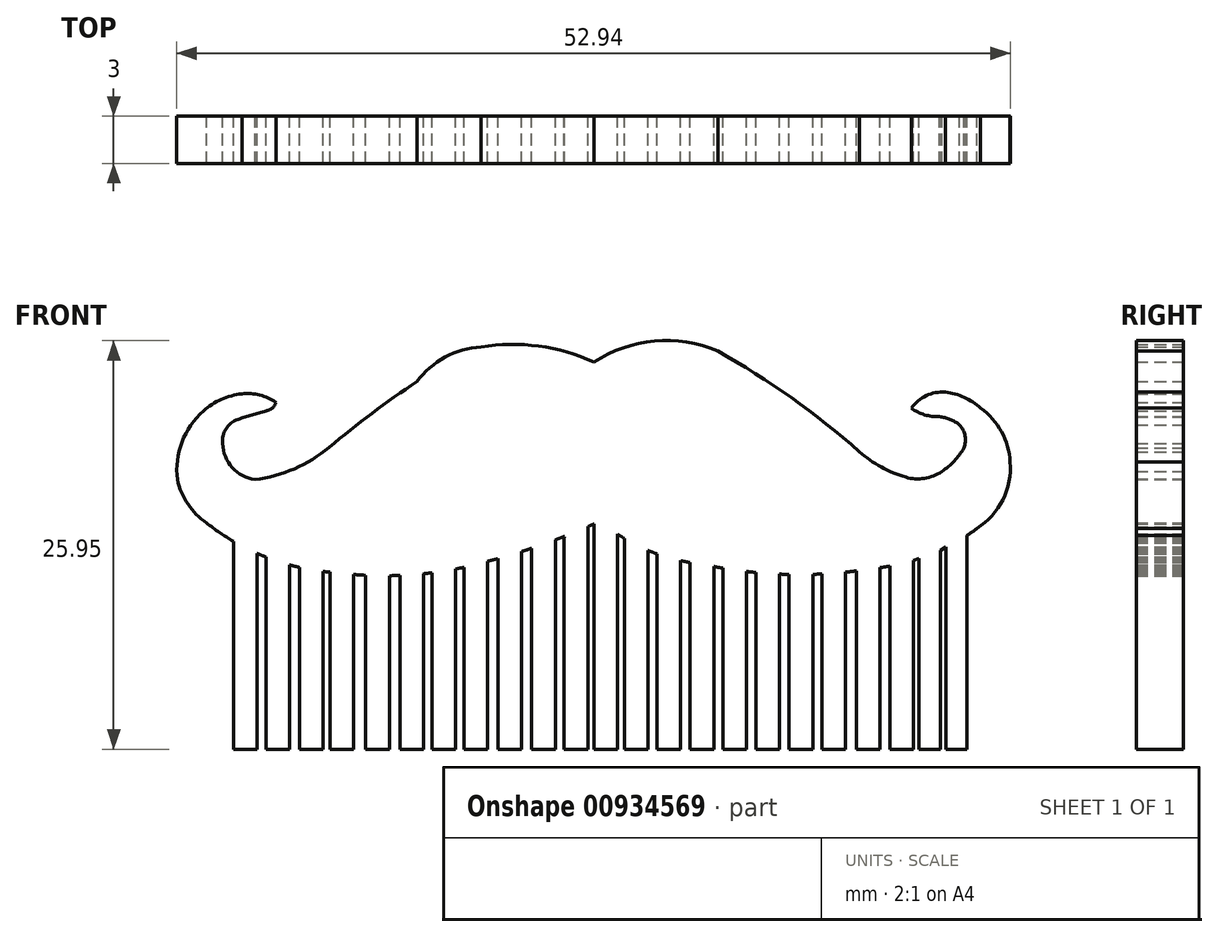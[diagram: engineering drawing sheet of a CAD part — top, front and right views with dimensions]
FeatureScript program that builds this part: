
annotation { "Feature Type Name" : "Feature", "Feature Type Description" : "" }
export const myFeature = defineFeature(function(context is Context, id is Id, definition is map)
    precondition{}
    {
        {
            var Q0;
            Q0=qCreatedBy(makeId("Front.planeOp"),FACE);
            var sketch = newSketch(context, id + "F0", { "sketchPlane" : qUnion([Q0])});
            skArc(sketch, "E0", {"start": v(10.65, 7.83) * mm, "mid": v(6.63, 8.47) * mm, "end": v(2.79, 7.13) * mm});
            skArc(sketch, "E1", {"start": v(2.79, 7.13) * mm, "mid": v(-0.72, 8.15) * mm, "end": v(-4.38, 8.1) * mm});
            skArc(sketch, "E2", {"start": v(-4.38, 8.1) * mm, "mid": v(-6.67, 7.45) * mm, "end": v(-8.46, 5.9) * mm});
            skArc(sketch, "E3", {"start": v(-8.46, 5.9) * mm, "mid": v(-11.3, 3.88) * mm, "end": v(-14.03, 1.72) * mm});
            skArc(sketch, "E4", {"start": v(-18.74, -0.33) * mm, "mid": v(-16.24, 0.36) * mm, "end": v(-14.03, 1.72) * mm});
            skArc(sketch, "E5", {"start": v(-20.8, 1.96) * mm, "mid": v(-20.18, 0.44) * mm, "end": v(-18.74, -0.33) * mm});
            skArc(sketch, "E6", {"start": v(-19.83, 3.5) * mm, "mid": v(-20.58, 2.9) * mm, "end": v(-20.8, 1.96) * mm});
            skArc(sketch, "E7", {"start": v(-18.03, 4.04) * mm, "mid": v(-18.94, 3.78) * mm, "end": v(-19.83, 3.5) * mm});
            skArc(sketch, "E8", {"start": v(-18.03, 4.04) * mm, "mid": v(-17.64, 4.22) * mm, "end": v(-17.4, 4.58) * mm});
            skArc(sketch, "E9", {"start": v(-17.4, 4.58) * mm, "mid": v(-18.44, 5.05) * mm, "end": v(-19.57, 5.12) * mm});
            skArc(sketch, "E10", {"start": v(-19.57, 5.12) * mm, "mid": v(-20.88, 4.78) * mm, "end": v(-22.02, 4.04) * mm});
            skArc(sketch, "E11", {"start": v(-22.02, 4.04) * mm, "mid": v(-23.38, 2.05) * mm, "end": v(-23.67, -0.33) * mm});
            skArc(sketch, "E12", {"start": v(-23.67, -0.33) * mm, "mid": v(-23, -1.88) * mm, "end": v(-21.82, -3.08) * mm});
            skArc(sketch, "E13", {"start": v(-21.82, -3.08) * mm, "mid": v(-20.98, -3.7) * mm, "end": v(-20.11, -4.24) * mm});
            skArc(sketch, "E14", {"start": v(-12.47, -6.36) * mm, "mid": v(-12.09, -6.38) * mm, "end": v(-11.7, -6.4) * mm});
            skArc(sketch, "E15", {"start": v(-3.96, -5.52) * mm, "mid": v(-3.63, -5.43) * mm, "end": v(-3.3, -5.34) * mm});
            skArc(sketch, "E16", {"start": v(4.29, -3.8) * mm, "mid": v(4.5, -3.93) * mm, "end": v(4.73, -4.07) * mm});
            skArc(sketch, "E17", {"start": v(10.4, -5.84) * mm, "mid": v(10.68, -5.9) * mm, "end": v(10.97, -5.95) * mm});
            skArc(sketch, "E18", {"start": v(20.96, -5.92) * mm, "mid": v(21.26, -5.88) * mm, "end": v(21.57, -5.83) * mm});
            skArc(sketch, "E19", {"start": v(27.11, -3.43) * mm, "mid": v(28.75, -1.6) * mm, "end": v(29.22, 0.8) * mm});
            skArc(sketch, "E20", {"start": v(29.22, 0.8) * mm, "mid": v(28.67, 2.72) * mm, "end": v(27.35, 4.2) * mm});
            skArc(sketch, "E21", {"start": v(27.35, 4.2) * mm, "mid": v(26.3, 4.9) * mm, "end": v(25.1, 5.24) * mm});
            skArc(sketch, "E22", {"start": v(25.1, 5.24) * mm, "mid": v(23.9, 5) * mm, "end": v(22.95, 4.2) * mm});
            skArc(sketch, "E23", {"start": v(22.95, 4.2) * mm, "mid": v(23.8, 3.8) * mm, "end": v(24.73, 3.67) * mm});
            skArc(sketch, "E24", {"start": v(26.01, 3.16) * mm, "mid": v(25.4, 3.5) * mm, "end": v(24.73, 3.67) * mm});
            skArc(sketch, "E25", {"start": v(26.28, 1.68) * mm, "mid": v(26.36, 2.46) * mm, "end": v(26.01, 3.16) * mm});
            skArc(sketch, "E26", {"start": v(24.88, 0.2) * mm, "mid": v(25.67, 0.85) * mm, "end": v(26.28, 1.68) * mm});
            skArc(sketch, "E27", {"start": v(22.6, -0.17) * mm, "mid": v(23.78, -0.25) * mm, "end": v(24.88, 0.2) * mm});
            skArc(sketch, "E28", {"start": v(19.65, 1.43) * mm, "mid": v(21.03, 0.47) * mm, "end": v(22.6, -0.17) * mm});
            skArc(sketch, "E29", {"start": v(19.65, 1.43) * mm, "mid": v(15.32, 4.88) * mm, "end": v(10.65, 7.83) * mm});
            skLineSegment(sketch, "E30", {"start": v(4.73, -4.07) * mm, "end": v(4.73, -17.45) * mm});
            skLineSegment(sketch, "E31", {"start": v(6.23, -17.45) * mm, "end": v(6.23, -4.82) * mm});
            skLineSegment(sketch, "E32", {"start": v(8.9, -17.45) * mm, "end": v(8.9, -5.55) * mm});
            skLineSegment(sketch, "E33", {"start": v(10.4, -17.45) * mm, "end": v(10.4, -5.84) * mm});
            skLineSegment(sketch, "E34", {"start": v(13.07, -17.45) * mm, "end": v(13.07, -6.23) * mm});
            skLineSegment(sketch, "E35", {"start": v(14.58, -17.45) * mm, "end": v(14.58, -6.33) * mm});
            skLineSegment(sketch, "E36", {"start": v(17.28, -17.45) * mm, "end": v(17.28, -6.36) * mm});
            skLineSegment(sketch, "E37", {"start": v(18.78, -17.45) * mm, "end": v(18.78, -6.2) * mm});
            skLineSegment(sketch, "E38", {"start": v(21.57, -17.45) * mm, "end": v(21.57, -5.82) * mm});
            skLineSegment(sketch, "E39", {"start": v(23.07, -17.45) * mm, "end": v(23.07, -5.47) * mm});
            skLineSegment(sketch, "E40", {"start": v(26.46, -17.45) * mm, "end": v(26.46, -4.36) * mm});
            skLineSegment(sketch, "E41.MirrorCS", {"start": v(2.4, -3.32) * mm, "end": v(2.4, -17.45) * mm});
            skLineSegment(sketch, "E42.MirrorCS", {"start": v(0.9, -17.45) * mm, "end": v(0.9, -4.04) * mm});
            skLineSegment(sketch, "E43.MirrorCS", {"start": v(-1.8, -17.45) * mm, "end": v(-1.8, -4.9) * mm});
            skLineSegment(sketch, "E44.MirrorCS", {"start": v(-6, -17.45) * mm, "end": v(-6, -6.04) * mm});
            skLineSegment(sketch, "E45.MirrorCS", {"start": v(-7.5, -17.45) * mm, "end": v(-7.5, -6.23) * mm});
            skLineSegment(sketch, "E46.MirrorCS", {"start": v(-10.2, -17.45) * mm, "end": v(-10.2, -6.36) * mm});
            skLineSegment(sketch, "E47.MirrorCS", {"start": v(-11.7, -17.45) * mm, "end": v(-11.7, -6.32) * mm});
            skLineSegment(sketch, "E48.MirrorCS", {"start": v(-14.4, -17.45) * mm, "end": v(-14.4, -6.16) * mm});
            skLineSegment(sketch, "E49.MirrorCS", {"start": v(-15.9, -17.45) * mm, "end": v(-15.9, -5.9) * mm});
            skLineSegment(sketch, "E50.MirrorCS", {"start": v(-20.1, -17.45) * mm, "end": v(-20.1, -4.36) * mm});
            skLineSegment(sketch, "E51", {"start": v(-20.1, -4.36) * mm, "end": v(-20.11, -4.24) * mm});
            skLineSegment(sketch, "E52", {"start": v(-6, -6.04) * mm, "end": v(-6, -6) * mm});
            skLineSegment(sketch, "E53", {"start": v(26.46, -4.36) * mm, "end": v(26.46, -3.88) * mm});
            skLineSegment(sketch, "E54", {"start": v(0.9, -4.04) * mm, "end": v(0.91, -3.93) * mm});
            skArc(sketch, "E55.trimOffspring", {"start": v(2.4, -3.32) * mm, "mid": v(2.6, -3.23) * mm, "end": v(2.79, -3.14) * mm});
            skArc(sketch, "E56.trimOffspring", {"start": v(6.23, -4.82) * mm, "mid": v(6.5, -4.94) * mm, "end": v(6.78, -5.04) * mm});
            skArc(sketch, "E57.trimOffspring", {"start": v(-1.8, -4.9) * mm, "mid": v(-1.49, -4.8) * mm, "end": v(-1.17, -4.69) * mm});
            skArc(sketch, "E58.trimOffspring", {"start": v(-6, -6) * mm, "mid": v(-5.74, -5.95) * mm, "end": v(-5.47, -5.9) * mm});
            skArc(sketch, "E59.trimOffspring", {"start": v(-10.2, -6.43) * mm, "mid": v(-9.87, -6.43) * mm, "end": v(-9.53, -6.41) * mm});
            skArc(sketch, "E60.trimOffspring", {"start": v(-14.4, -6.16) * mm, "mid": v(-14.19, -6.19) * mm, "end": v(-13.97, -6.2) * mm});
            skArc(sketch, "E61.trimOffspring", {"start": v(-18.6, -5.01) * mm, "mid": v(-18.32, -5.13) * mm, "end": v(-18.04, -5.25) * mm});
            skArc(sketch, "E62.trimOffspring", {"start": v(14.58, -6.33) * mm, "mid": v(14.88, -6.34) * mm, "end": v(15.18, -6.35) * mm});
            skLineSegment(sketch, "E63", {"start": v(17.28, -6.36) * mm, "end": v(17.28, -6.3) * mm});
            skPoint(sketch, "E63.endSnap0", {"position": v(17.6, -6.3) * mm});
            skArc(sketch, "E64.trimOffspring", {"start": v(18.78, -6.2) * mm, "mid": v(19.11, -6.17) * mm, "end": v(19.45, -6.13) * mm});
            skArc(sketch, "E65.trimOffspring", {"start": v(26.46, -3.88) * mm, "mid": v(26.79, -3.66) * mm, "end": v(27.11, -3.43) * mm});
            skPoint(sketch, "E66.orphan", {"position": v(-3.3, -27.97) * mm});
            skPoint(sketch, "E67.orphan", {"position": v(2.4, -27.97) * mm});
            skPoint(sketch, "E68.start.orphan", {"position": v(4.73, -27.97) * mm});
            skPoint(sketch, "E69.start.orphan", {"position": v(24.96, -27.97) * mm});
            skLineSegment(sketch, "E70", {"start": v(-18.03, -17.45) * mm, "end": v(-16.53, -17.45) * mm});
            skLineSegment(sketch, "E71", {"start": v(-18.6, -17.45) * mm, "end": v(-20.1, -17.45) * mm});
            skLineSegment(sketch, "E72.trimOffspring", {"start": v(-15.9, -17.45) * mm, "end": v(-14.4, -17.45) * mm});
            skArc(sketch, "E73.trimOffspring", {"start": v(-16.53, -5.75) * mm, "mid": v(-16.22, -5.83) * mm, "end": v(-15.9, -5.9) * mm});
            skLineSegment(sketch, "E74", {"start": v(-16.53, -5.75) * mm, "end": v(-16.53, -17.45) * mm});
            skPoint(sketch, "E75.MirrorCS.end.orphan", {"position": v(-18.03, -5.33) * mm});
            skLineSegment(sketch, "E76", {"start": v(-18.6, -5.01) * mm, "end": v(-18.6, -17.45) * mm});
            skLineSegment(sketch, "E77", {"start": v(-18.03, -17.45) * mm, "end": v(-18.04, -5.25) * mm});
            skLineSegment(sketch, "E78.trimOffspring", {"start": v(-11.7, -17.45) * mm, "end": v(-10.2, -17.45) * mm});
            skLineSegment(sketch, "E79", {"start": v(-13.97, -17.45) * mm, "end": v(-12.47, -17.45) * mm});
            skLineSegment(sketch, "E80", {"start": v(-12.47, -6.36) * mm, "end": v(-12.47, -17.45) * mm});
            skLineSegment(sketch, "E81", {"start": v(-13.97, -17.45) * mm, "end": v(-13.97, -6.2) * mm});
            skLineSegment(sketch, "E82", {"start": v(-9.53, -17.45) * mm, "end": v(-8.03, -17.45) * mm});
            skLineSegment(sketch, "E83", {"start": v(-8.03, -6.3) * mm, "end": v(-8.03, -17.45) * mm});
            skLineSegment(sketch, "E84", {"start": v(-9.53, -17.45) * mm, "end": v(-9.53, -6.41) * mm});
            skLineSegment(sketch, "E85.trimOffspring", {"start": v(-7.5, -17.45) * mm, "end": v(-6, -17.45) * mm});
            skArc(sketch, "E86.trimOffspring", {"start": v(-8.03, -6.3) * mm, "mid": v(-7.77, -6.28) * mm, "end": v(-7.5, -6.24) * mm});
            skLineSegment(sketch, "E87", {"start": v(-5.46, -17.45) * mm, "end": v(-3.96, -17.45) * mm});
            skLineSegment(sketch, "E88", {"start": v(-5.46, -17.45) * mm, "end": v(-5.47, -5.9) * mm});
            skLineSegment(sketch, "E89.trimOffspring", {"start": v(-3.3, -17.45) * mm, "end": v(-1.8, -17.45) * mm});
            skLineSegment(sketch, "E90", {"start": v(-1.16, -17.45) * mm, "end": v(0.34, -17.45) * mm});
            skLineSegment(sketch, "E91", {"start": v(-1.16, -17.45) * mm, "end": v(-1.17, -4.69) * mm});
            skLineSegment(sketch, "E92.trimOffspring", {"start": v(0.9, -17.45) * mm, "end": v(2.4, -17.45) * mm});
            skArc(sketch, "E93.trimOffspring", {"start": v(0.34, -4.15) * mm, "mid": v(0.62, -4.04) * mm, "end": v(0.91, -3.93) * mm});
            skLineSegment(sketch, "E94", {"start": v(-3.96, -5.52) * mm, "end": v(-3.96, -17.45) * mm});
            skLineSegment(sketch, "E95", {"start": v(-3.3, -17.45) * mm, "end": v(-3.3, -5.34) * mm});
            skLineSegment(sketch, "E96", {"start": v(0.34, -4.15) * mm, "end": v(0.34, -17.45) * mm});
            skLineSegment(sketch, "E97", {"start": v(2.79, -17.45) * mm, "end": v(4.29, -17.45) * mm});
            skPoint(sketch, "E98", {"position": v(2.79, -3.14) * mm});
            skLineSegment(sketch, "E99", {"start": v(4.29, -17.45) * mm, "end": v(4.29, -3.8) * mm});
            skLineSegment(sketch, "E100", {"start": v(2.79, -17.45) * mm, "end": v(2.79, -3.14) * mm});
            skLineSegment(sketch, "E101.trimOffspring", {"start": v(4.73, -17.45) * mm, "end": v(6.23, -17.45) * mm});
            skLineSegment(sketch, "E102", {"start": v(6.78, -17.45) * mm, "end": v(8.28, -17.45) * mm});
            skLineSegment(sketch, "E103", {"start": v(6.78, -17.45) * mm, "end": v(6.78, -5.04) * mm});
            skLineSegment(sketch, "E104", {"start": v(8.28, -17.45) * mm, "end": v(8.28, -5.48) * mm});
            skArc(sketch, "E105.trimOffspring", {"start": v(8.28, -5.48) * mm, "mid": v(8.59, -5.54) * mm, "end": v(8.9, -5.6) * mm});
            skLineSegment(sketch, "E106.trimOffspring", {"start": v(8.9, -17.45) * mm, "end": v(10.4, -17.45) * mm});
            skLineSegment(sketch, "E107", {"start": v(10.97, -17.45) * mm, "end": v(12.47, -17.45) * mm});
            skLineSegment(sketch, "E108", {"start": v(12.47, -6.16) * mm, "end": v(12.47, -17.45) * mm});
            skLineSegment(sketch, "E109", {"start": v(10.97, -17.45) * mm, "end": v(10.97, -5.95) * mm});
            skArc(sketch, "E110.trimOffspring", {"start": v(12.47, -6.16) * mm, "mid": v(12.77, -6.2) * mm, "end": v(13.07, -6.23) * mm});
            skLineSegment(sketch, "E111.trimOffspring", {"start": v(13.07, -17.45) * mm, "end": v(14.58, -17.45) * mm});
            skLineSegment(sketch, "E112", {"start": v(15.18, -17.45) * mm, "end": v(16.68, -17.45) * mm});
            skLineSegment(sketch, "E113", {"start": v(16.68, -6.34) * mm, "end": v(16.68, -17.45) * mm});
            skLineSegment(sketch, "E114", {"start": v(15.18, -17.45) * mm, "end": v(15.18, -6.35) * mm});
            skArc(sketch, "E115.trimOffspring", {"start": v(16.68, -6.34) * mm, "mid": v(16.98, -6.33) * mm, "end": v(17.28, -6.32) * mm});
            skLineSegment(sketch, "E116", {"start": v(19.46, -17.45) * mm, "end": v(20.96, -17.45) * mm});
            skLineSegment(sketch, "E117", {"start": v(20.96, -5.92) * mm, "end": v(20.96, -17.45) * mm});
            skLineSegment(sketch, "E118", {"start": v(19.46, -17.45) * mm, "end": v(19.45, -6.13) * mm});
            skPoint(sketch, "E119.orphan", {"position": v(19.45, -5.25) * mm});
            skLineSegment(sketch, "E120", {"start": v(17.28, -17.45) * mm, "end": v(18.78, -17.45) * mm});
            skLineSegment(sketch, "E121.trimOffspring", {"start": v(21.57, -17.45) * mm, "end": v(23.07, -17.45) * mm});
            skLineSegment(sketch, "E122", {"start": v(23.43, -17.45) * mm, "end": v(24.78, -17.45) * mm});
            skLineSegment(sketch, "E123", {"start": v(24.78, -17.45) * mm, "end": v(24.78, -4.82) * mm});
            skLineSegment(sketch, "E124.trimOffspring", {"start": v(25.14, -17.45) * mm, "end": v(26.46, -17.45) * mm});
            skLineSegment(sketch, "E125", {"start": v(23.43, -17.45) * mm, "end": v(23.43, -5.33) * mm});
            skLineSegment(sketch, "E126", {"start": v(23.07, -5.47) * mm, "end": v(23.43, -5.33) * mm});
            skLineSegment(sketch, "E127", {"start": v(25.14, -17.45) * mm, "end": v(25.14, -4.62) * mm});
            skLineSegment(sketch, "E128", {"start": v(24.78, -4.82) * mm, "end": v(25.14, -4.62) * mm});
            skSolve(sketch);
        }
        {
            var Q0;
            Q0=makeQuery(id+"F0.imprint","IMPRINT",FACE,{"disambiguationData":[TD([[makeQuery(id+"F0.imprint","IMPRINT",EDGE,{"derivedFrom":sQuery(id+"F0.wireOp",EDGE,"E0")}),1.0]])]});
            extrude(context, id + "F1", {"entities" : qUnion([Q0]), "depth" : 3 * mm, "offsetDistance" : 25 * mm});
        }
    });
